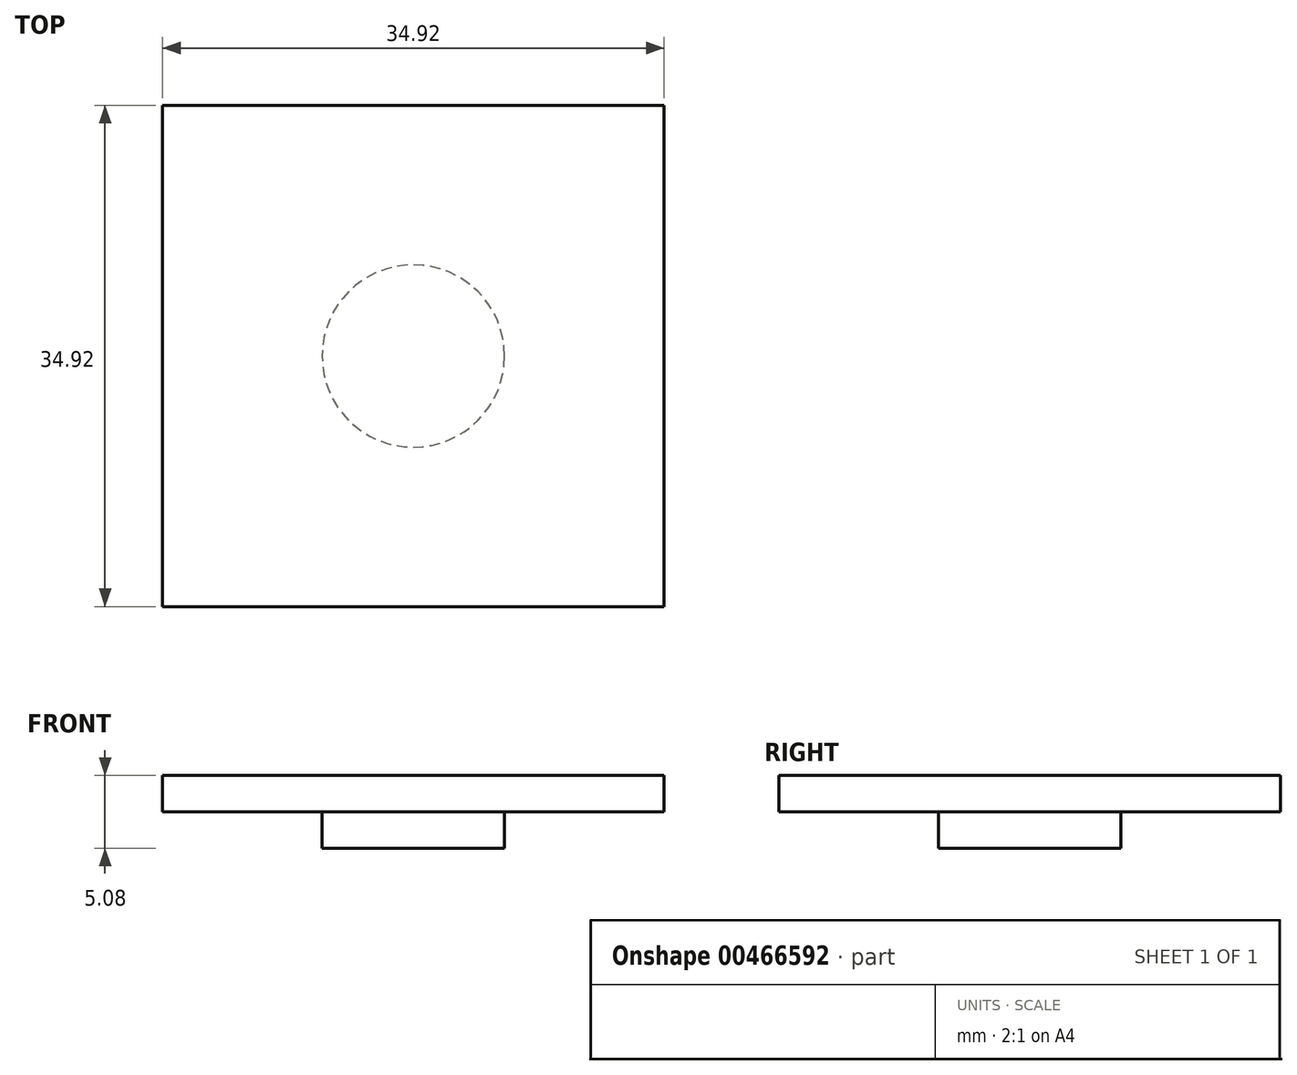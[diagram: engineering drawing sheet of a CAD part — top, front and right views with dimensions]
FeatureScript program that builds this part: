
annotation { "Feature Type Name" : "Feature", "Feature Type Description" : "" }
export const myFeature = defineFeature(function(context is Context, id is Id, definition is map)
    precondition{}
    {
        {
            var Q0;
            Q0=qCreatedBy(makeId("Top.planeOp"),FACE);
            var sketch = newSketch(context, id + "F0", { "sketchPlane" : qUnion([Q0])});
            skLineSegment(sketch, "E0.bottom", {"start": v(0, 0) * mm, "end": v(-34.93, 0) * mm});
            skLineSegment(sketch, "E0.top", {"start": v(0, 34.93) * mm, "end": v(-34.93, 34.93) * mm});
            skLineSegment(sketch, "E0.left", {"start": v(0, 0) * mm, "end": v(0, 34.93) * mm});
            skLineSegment(sketch, "E0.right", {"start": v(-34.93, 0) * mm, "end": v(-34.93, 34.92) * mm});
            skSolve(sketch);
        }
        {
            var Q0;
            Q0 = qSketchRegion(id + "F0", true);
            var Q1;
            Q1=makeQuery(id+"F0.imprint","IMPRINT",FACE,{"disambiguationData":[TD([[makeQuery(id+"F0.imprint","IMPRINT",EDGE,{"derivedFrom":sQuery(id+"F0.wireOp",EDGE,"E0.bottom")}),-1.0]])]});
            extrude(context, id + "F1", {"entities" : qUnion([Q0, Q1]), "depth" : 2.54 * mm});
        }
        {
            var Q0;
            Q0=makeQuery(id+"F1.opExtrude","CAP_FACE",FACE,{"disambiguationData":[OSD([sQuery(id+"F0.wireOp",EDGE,"E0.bottom"),sQuery(id+"F0.wireOp",EDGE,"E0.top"),sQuery(id+"F0.wireOp",EDGE,"E0.left"),sQuery(id+"F0.wireOp",EDGE,"E0.right")])],"isStart":true});
            var sketch = newSketch(context, id + "F2", { "sketchPlane" : qUnion([Q0])});
            skCircle(sketch, "E1", {"center": v(-17.46, -17.46) * mm, "radius": 6.35 * mm});
            skPoint(sketch, "E2.orphan", {"position": v(-34.93, -34.92) * mm});
            skPoint(sketch, "E3.start.orphan", {"position": v(0, 0) * mm});
            skSolve(sketch);
        }
        {
            var Q0;
            Q0 = qSketchRegion(id + "F2", true);
            var Q1;
            Q1=makeQuery(id+"F2.imprint","IMPRINT",FACE,{"disambiguationData":[TD([[makeQuery(id+"F2.imprint","IMPRINT",EDGE,{"derivedFrom":sQuery(id+"F2.wireOp",EDGE,"E1")}),1.0]])]});
            extrude(context, id + "F3", {"entities" : qUnion([Q0, Q1]), "operationType" : NewBodyOperationType.ADD, "depth" : 2.54 * mm});
        }
    });
